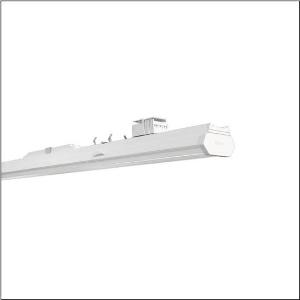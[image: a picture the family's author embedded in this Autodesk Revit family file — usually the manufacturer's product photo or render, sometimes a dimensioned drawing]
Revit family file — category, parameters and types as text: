
# Revit family: licross_11_protected_mo_51tp12dn495g3s
name_source: partatom
category: Lighting Fixtures
units: mm (PartAtom-declared; Revit-internal decimal feet)

## family parameters
Cut with Voids When Loaded = No
Host = Face
Light Source = No
Part Type = Normal
Room Calculation Point = No
Round Connector Dimension = Use Diameter
Shared = No

## types (1)
- --- (1 x LED, 980 lm, 6.8 W, 4000K)
    Apparent Load = 7 VA
    CIE Flux Codes = 73 92 98 99 100
    Color Rendering = 80
    Color Temperature = 4000K
    Default Elevation = 1800 mm
    Description = Licross 11 Protected MO, luminaire insert, of sheet steel, galvanised, coil coated, white, length: 1.500mm, width: 90mm, height: 101mm, LED rated luminous flux: 9.980lm, light colour: 840, SDCM (Standard Deviation of Colour Matching)MacAdam ≤ 2 SDCM (initial), control gear: DALI 2 (for two DALI lines), with plug, 6-pole, with phase selection, for trunking rail, 14-core, mains connection: 220..240V, AC, 50/60Hz, rated input power: 61W, for trunking rail, 14-core, internal wiring halogen-free, for emergency light function, converter,control gear: single battery element, battery: LiFePO4, 9Ah, primary light control with lens, of plastic, primary optical cover: cover, of PMMA, light emission: direct distribution, primary light characteristic: symmetric, protection rating (complete): IP64, insulation class (complete): insulation class I (protective earthing), certification: CE, UKCA, protection symbol: D if used in an environment with conductive dust loads with corresponding accessories, impact resistance: IK06, permissible ambient temperature for indoor applications: +5..+35°C, standard: EN 60598-2-22, LABS conformity tested according to VDMA 24364:2018-05, reducing of maximum allowable ambient temperature of 5°C with ceiling mounting, corresponds to IFS (International Featured Standards) requirements for safety and quality in the food industry, The light source and the operating device comply with the requirements of the Ecodesign Regulation (EU) 2019/2020 and are replaceable in accordance with this regulation, packaging unit: 1 piece
    Height = 92 mm
    Lamp = 1 x LED
    Lamp Light Flux = 980 lm
    Lamp Power = 6.8 W
    Lamp count = 1
    Length = 1500 mm
    Luminous efficacy = 144 lm/W
    Manufacturer = Siteco
    ModVariant = No
    Model = 51TP12DN495G3S
    Mounting Place = Ceiling
    Mounting Type = Pendant
    Number of Poles = 1
    OnlyDefault = Yes
    Power Factor = 1
    Product Name = Licross 11 Protected MO
    Product group = luminaire insert | ceiling pendant
    ProductGroupID = 901
    Protection Class = Protection class I
    Protection Degree = IP 64
    RLX_Detail_Level = 1
    RLX_Emergency_Light_Flux = 0 lm
    RLX_Emergency_Type = 0
    RLX_Emergency_Type_DB = No
    RlxData = <blob elided: 24937 chars, md5=8fe49d76>
    Socket = socket
    Standby Power = 0 W
    System Light Flux = 980 lm
    System Power = 7 W
    Type Comments = : emergency light operation: 3 h
    Type Image = l_1256148.jpg
    URL = http://relux.com
    VarID = @adj_096167
    Voltage = 0 V
    Weight = 0.00 kg
    Width = 88 mm

## geometry (parser evidence)
native form markers: Blend x4, Sweep x10
no freeform markers — native parametric forms only
